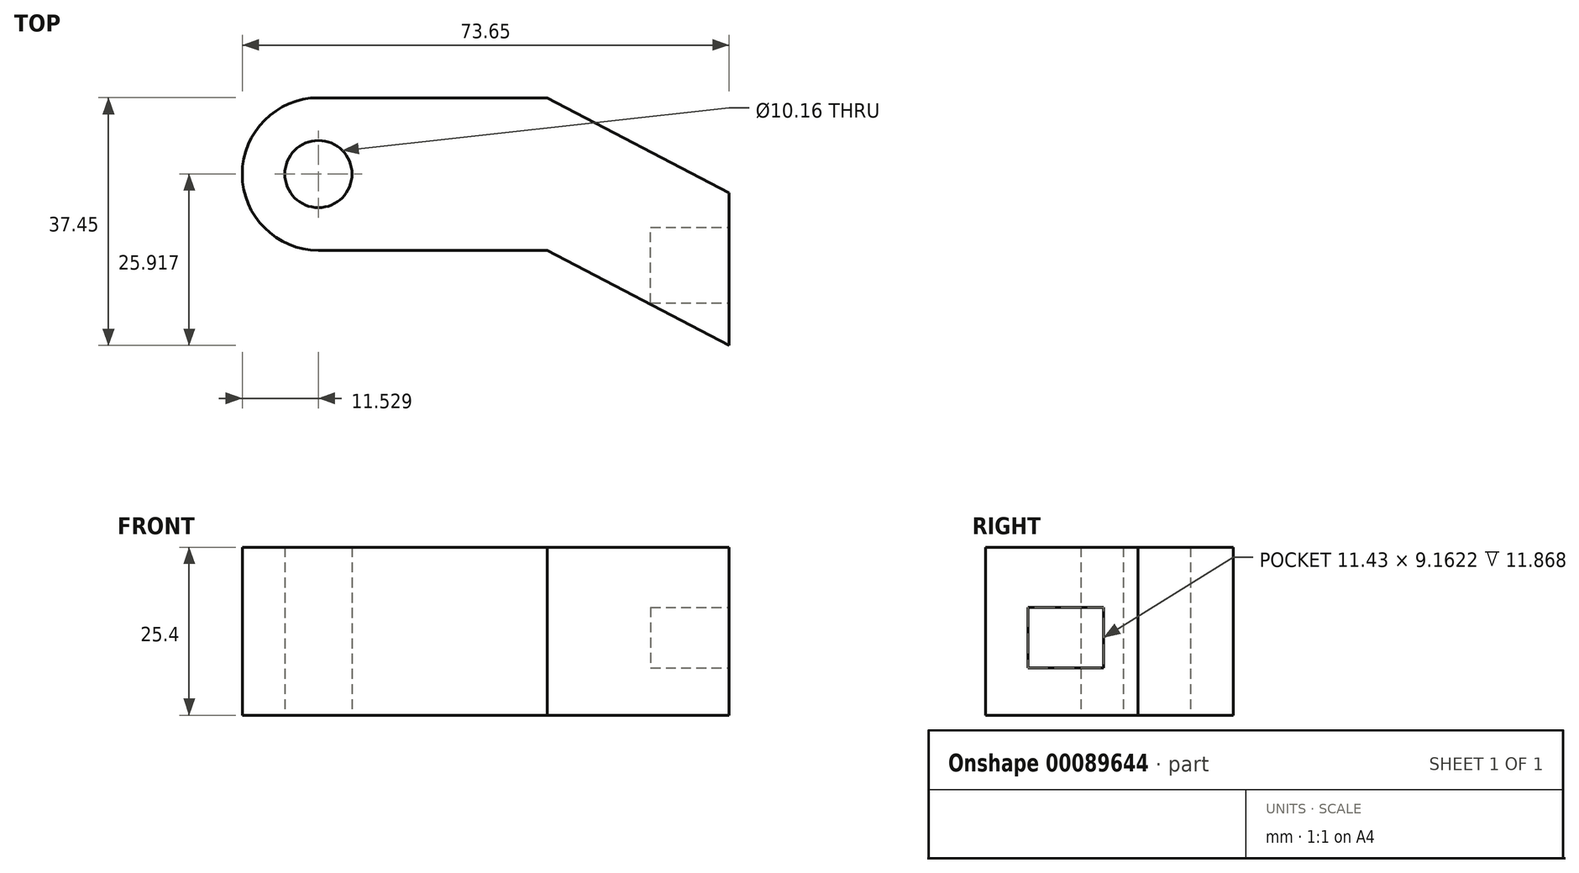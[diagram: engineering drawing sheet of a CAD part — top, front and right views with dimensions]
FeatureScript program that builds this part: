
annotation { "Feature Type Name" : "Feature", "Feature Type Description" : "" }
export const myFeature = defineFeature(function(context is Context, id is Id, definition is map)
    precondition{}
    {
        {
            var Q0;
            Q0=qCreatedBy(makeId("Top.planeOp"),FACE);
            var sketch = newSketch(context, id + "F0", { "sketchPlane" : qUnion([Q0])});
            skLineSegment(sketch, "E0", {"start": v(-34.58, -10.11) * mm, "end": v(0, -10.11) * mm});
            skLineSegment(sketch, "E1", {"start": v(0, -10.11) * mm, "end": v(27.54, -24.5) * mm});
            skLineSegment(sketch, "E2", {"start": v(-34.58, 12.95) * mm, "end": v(0, 12.95) * mm});
            skLineSegment(sketch, "E3", {"start": v(0, 12.95) * mm, "end": v(27.54, -1.44) * mm});
            skLineSegment(sketch, "E4", {"start": v(27.54, -1.44) * mm, "end": v(27.54, -24.5) * mm});
            skArc(sketch, "E5", {"start": v(-34.58, 12.95) * mm, "mid": v(-46.11, 1.42) * mm, "end": v(-34.58, -10.11) * mm});
            skCircle(sketch, "E6", {"center": v(-34.58, 1.42) * mm, "radius": 5.08 * mm});
            skSolve(sketch);
        }
        {
            var Q0;
            Q0=makeQuery(id+"F0.imprint","IMPRINT",FACE,{"disambiguationData":[TD([[makeQuery(id+"F0.imprint","IMPRINT",EDGE,{"derivedFrom":sQuery(id+"F0.wireOp",EDGE,"E0")}),1.0]])]});
            extrude(context, id + "F1", {"entities" : qUnion([Q0]), "depth" : 25.4 * mm});
        }
        {
            var Q0;
            Q0=makeQuery(id+"F1.opExtrude","SWEPT_FACE",FACE,{"disambiguationData":[OSD([sQuery(id+"F0.wireOp",EDGE,"E4")])]});
            var sketch = newSketch(context, id + "F2", { "sketchPlane" : qUnion([Q0])});
            skLineSegment(sketch, "E7.bottom", {"start": v(-18.1, 16.32) * mm, "end": v(-6.66, 16.32) * mm});
            skLineSegment(sketch, "E7.top", {"start": v(-18.1, 7.15) * mm, "end": v(-6.66, 7.15) * mm});
            skLineSegment(sketch, "E7.left", {"start": v(-18.1, 16.32) * mm, "end": v(-18.1, 7.15) * mm});
            skLineSegment(sketch, "E7.right", {"start": v(-6.66, 16.32) * mm, "end": v(-6.66, 7.15) * mm});
            skPoint(sketch, "E8", {"position": v(-12.38, 11.51) * mm});
            skPoint(sketch, "E8.positionSnap0", {"position": v(-12.38, 7.15) * mm});
            skLineSegment(sketch, "E9.2.0.0", {"start": v(93.34, 16.32) * mm, "end": v(93.34, 7.15) * mm});
            skSolve(sketch);
        }
        {
            var Q0;
            Q0=makeQuery(id+"F2.imprint","IMPRINT",FACE,{"disambiguationData":[TD([[makeQuery(id+"F2.imprint","IMPRINT",EDGE,{"derivedFrom":sQuery(id+"F2.wireOp",EDGE,"E7.bottom")}),-1.0]])]});
            extrude(context, id + "F3", {"entities" : qUnion([Q0]), "operationType" : NewBodyOperationType.REMOVE, "oppositeDirection" : true, "depth" : 11.87 * mm});
        }
    });
